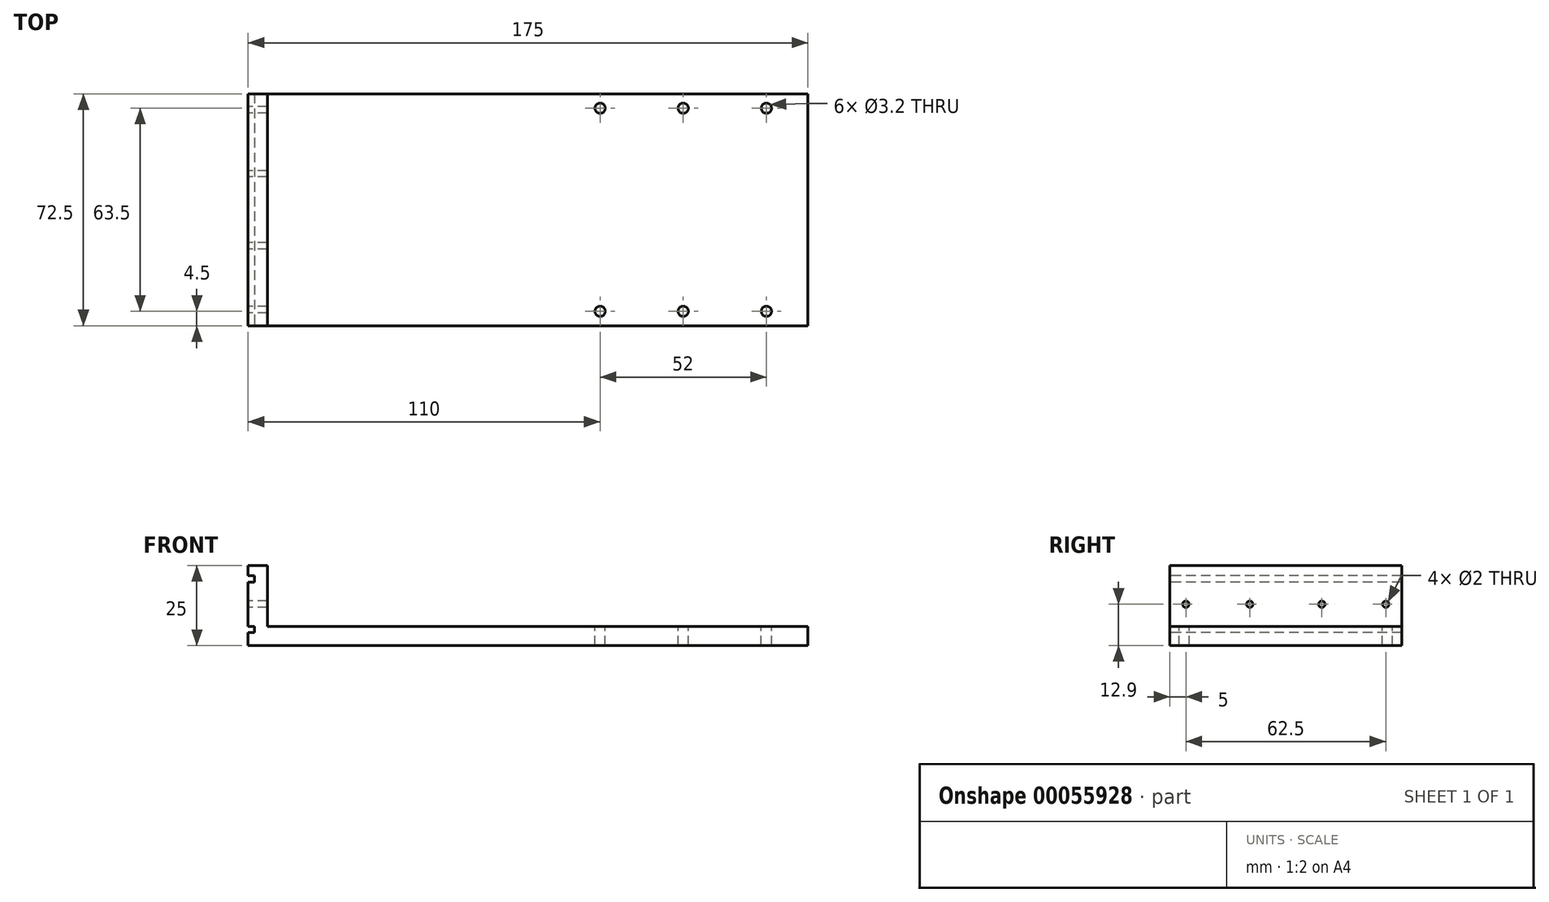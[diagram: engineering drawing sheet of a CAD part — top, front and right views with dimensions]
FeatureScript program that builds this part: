
annotation { "Feature Type Name" : "Feature", "Feature Type Description" : "" }
export const myFeature = defineFeature(function(context is Context, id is Id, definition is map)
    precondition{}
    {
        {
            var Q0;
            Q0=qCreatedBy(makeId("Top.planeOp"),FACE);
            var sketch = newSketch(context, id + "F0", { "sketchPlane" : qUnion([Q0])});
            skLineSegment(sketch, "E0.rect.bottom", {"start": v(87.5, -36.25) * mm, "end": v(-87.5, -36.25) * mm});
            skLineSegment(sketch, "E0.rect.top", {"start": v(87.5, 36.25) * mm, "end": v(-87.5, 36.25) * mm});
            skLineSegment(sketch, "E0.rect.left", {"start": v(87.5, -36.25) * mm, "end": v(87.5, 36.25) * mm});
            skLineSegment(sketch, "E0.rect.right", {"start": v(-87.5, -36.25) * mm, "end": v(-87.5, 36.25) * mm});
            skPoint(sketch, "E0.rect.middle", {"position": v(0, 0) * mm});
            skSolve(sketch);
        }
        {
            var Q0;
            Q0=makeQuery(id+"F0.imprint","IMPRINT",FACE,{"disambiguationData":[TD([[makeQuery(id+"F0.imprint","IMPRINT",EDGE,{"derivedFrom":sQuery(id+"F0.wireOp",EDGE,"E0.rect.bottom")}),-1.0]])]});
            extrude(context, id + "F1", {"entities" : qUnion([Q0]), "depth" : 25 * mm});
        }
        {
            var Q0;
            Q0=makeQuery(id+"F1.opExtrude","CAP_FACE",FACE,{"disambiguationData":[OSD([sQuery(id+"F0.wireOp",EDGE,"E0.rect.bottom"),sQuery(id+"F0.wireOp",EDGE,"E0.rect.top"),sQuery(id+"F0.wireOp",EDGE,"E0.rect.left"),sQuery(id+"F0.wireOp",EDGE,"E0.rect.right")])],"isStart":false});
            var sketch = newSketch(context, id + "F2", { "sketchPlane" : qUnion([Q0])});
            skLineSegment(sketch, "E1.bottom", {"start": v(87.5, 36.25) * mm, "end": v(-81.5, 36.25) * mm});
            skLineSegment(sketch, "E1.top", {"start": v(87.5, -36.25) * mm, "end": v(-81.5, -36.25) * mm});
            skLineSegment(sketch, "E1.left", {"start": v(87.5, 36.25) * mm, "end": v(87.5, -36.25) * mm});
            skLineSegment(sketch, "E1.right", {"start": v(-81.5, 36.25) * mm, "end": v(-81.5, -36.25) * mm});
            skSolve(sketch);
        }
        {
            var Q0;
            Q0=makeQuery(id+"F2.imprint","IMPRINT",FACE,{"disambiguationData":[TD([[makeQuery(id+"F2.imprint","IMPRINT",EDGE,{"derivedFrom":sQuery(id+"F2.wireOp",EDGE,"E1.bottom")}),1.0]])]});
            extrude(context, id + "F3", {"entities" : qUnion([Q0]), "operationType" : NewBodyOperationType.REMOVE, "oppositeDirection" : true, "depth" : 19 * mm});
        }
        {
            var Q0;
            Q0=makeQuery(id+"F3.boolean.opBoolean","COPY",FACE,{"derivedFrom":makeQuery(id+"F3.opExtrude","CAP_FACE",FACE,{"disambiguationData":[OSD([sQuery(id+"F2.wireOp",EDGE,"E1.bottom"),sQuery(id+"F2.wireOp",EDGE,"E1.top"),sQuery(id+"F2.wireOp",EDGE,"E1.left"),sQuery(id+"F2.wireOp",EDGE,"E1.right")])],"isStart":false})});
            var sketch = newSketch(context, id + "F4", { "sketchPlane" : qUnion([Q0])});
            skPoint(sketch, "E2", {"position": v(74.5, 31.75) * mm});
            skPoint(sketch, "E3", {"position": v(48.5, 31.75) * mm});
            skPoint(sketch, "E4", {"position": v(22.5, 31.75) * mm});
            skPoint(sketch, "E5.MirrorP", {"position": v(22.5, -31.75) * mm});
            skPoint(sketch, "E6.MirrorP", {"position": v(48.5, -31.75) * mm});
            skPoint(sketch, "E7.MirrorP", {"position": v(74.5, -31.75) * mm});
            skSolve(sketch);
        }
        {
            var Q0;
            Q0=sQuery(id+"F4.wireOp",VERTEX,"E4");
            var Q1;
            Q1=sQuery(id+"F4.wireOp",VERTEX,"E3");
            var Q2;
            Q2=sQuery(id+"F4.wireOp",VERTEX,"E2");
            var Q3;
            Q3=sQuery(id+"F4.wireOp",VERTEX,"E7.MirrorP");
            var Q4;
            Q4=sQuery(id+"F4.wireOp",VERTEX,"E6.MirrorP");
            var Q5;
            Q5=sQuery(id+"F4.wireOp",VERTEX,"E5.MirrorP");
            var Q6;
            Q6=makeQuery(id+"F1.opExtrude","SWEPT_BODY",BODY,{"disambiguationData":[OSD([sQuery(id+"F0.wireOp",EDGE,"E0.rect.bottom"),sQuery(id+"F0.wireOp",EDGE,"E0.rect.top"),sQuery(id+"F0.wireOp",EDGE,"E0.rect.left"),sQuery(id+"F0.wireOp",EDGE,"E0.rect.right")])]});
            hole(context, id + "F5", {"style" : HoleStyle.SIMPLE, "holeDiameter" : 3.2 * mm, "endStyle" : HoleEndStyle.THROUGH, "locations" : qUnion([Q0, Q1, Q2, Q3, Q4, Q5]), "scope" : qUnion([Q6])});
        }
        {
            var Q0;
            Q0=makeQuery(id+"F1.opExtrude","SWEPT_FACE",FACE,{"disambiguationData":[OSD([sQuery(id+"F0.wireOp",EDGE,"E0.rect.right")])]});
            var sketch = newSketch(context, id + "F6", { "sketchPlane" : qUnion([Q0])});
            skLineSegment(sketch, "E8.bottom", {"start": v(-36.25, 4) * mm, "end": v(36.25, 4) * mm});
            skLineSegment(sketch, "E8.top", {"start": v(-36.25, 6) * mm, "end": v(36.25, 6) * mm});
            skLineSegment(sketch, "E8.left", {"start": v(-36.25, 4) * mm, "end": v(-36.25, 6) * mm});
            skLineSegment(sketch, "E8.right", {"start": v(36.25, 4) * mm, "end": v(36.25, 6) * mm});
            skLineSegment(sketch, "E9.bottom", {"start": v(-36.25, 19.8) * mm, "end": v(36.25, 19.8) * mm});
            skLineSegment(sketch, "E9.top", {"start": v(-36.25, 21.8) * mm, "end": v(36.25, 21.8) * mm});
            skLineSegment(sketch, "E9.left", {"start": v(-36.25, 19.8) * mm, "end": v(-36.25, 21.8) * mm});
            skLineSegment(sketch, "E9.right", {"start": v(36.25, 19.8) * mm, "end": v(36.25, 21.8) * mm});
            skSolve(sketch);
        }
        {
            var Q0;
            Q0=makeQuery(id+"F6.imprint","IMPRINT",FACE,{"disambiguationData":[TD([[makeQuery(id+"F6.imprint","IMPRINT",EDGE,{"derivedFrom":sQuery(id+"F6.wireOp",EDGE,"E8.bottom")}),1.0]])]});
            var Q1;
            Q1=makeQuery(id+"F6.imprint","IMPRINT",FACE,{"disambiguationData":[TD([[makeQuery(id+"F6.imprint","IMPRINT",EDGE,{"derivedFrom":sQuery(id+"F6.wireOp",EDGE,"E9.bottom")}),1.0]])]});
            extrude(context, id + "F7", {"entities" : qUnion([Q0, Q1]), "operationType" : NewBodyOperationType.REMOVE, "oppositeDirection" : true, "depth" : 2 * mm});
        }
        {
            var Q0;
            Q0=makeQuery(id+"F7.boolean.opBoolean","SPLIT",FACE,{"disambiguationData":[TD([makeQuery(id+"F7.opExtrude","SWEPT_FACE",FACE,{"disambiguationData":[OSD([sQuery(id+"F6.wireOp",EDGE,"E8.top")])]})])],"derivedFrom":makeQuery(id+"F1.opExtrude","SWEPT_FACE",FACE,{"disambiguationData":[OSD([sQuery(id+"F0.wireOp",EDGE,"E0.rect.right")])]})});
            var sketch = newSketch(context, id + "F8", { "sketchPlane" : qUnion([Q0])});
            skPoint(sketch, "E10", {"position": v(-31.25, 12.9) * mm});
            skPoint(sketch, "E10.positionSnap0", {"position": v(-36.25, 12.9) * mm});
            skPoint(sketch, "E11", {"position": v(31.25, 12.9) * mm});
            skPoint(sketch, "E12", {"position": v(11.25, 12.9) * mm});
            skPoint(sketch, "E13", {"position": v(-11.25, 12.9) * mm});
            skSolve(sketch);
        }
        {
            var Q0;
            Q0=sQuery(id+"F8.wireOp",VERTEX,"E10");
            var Q1;
            Q1=sQuery(id+"F8.wireOp",VERTEX,"E13");
            var Q2;
            Q2=sQuery(id+"F8.wireOp",VERTEX,"E12");
            var Q3;
            Q3=sQuery(id+"F8.wireOp",VERTEX,"E11");
            var Q4;
            Q4=makeQuery(id+"F1.opExtrude","SWEPT_BODY",BODY,{"disambiguationData":[OSD([sQuery(id+"F0.wireOp",EDGE,"E0.rect.bottom"),sQuery(id+"F0.wireOp",EDGE,"E0.rect.top"),sQuery(id+"F0.wireOp",EDGE,"E0.rect.left"),sQuery(id+"F0.wireOp",EDGE,"E0.rect.right")])]});
            hole(context, id + "F9", {"style" : HoleStyle.SIMPLE, "holeDiameter" : 2 * mm, "endStyle" : HoleEndStyle.THROUGH, "locations" : qUnion([Q0, Q1, Q2, Q3]), "scope" : qUnion([Q4])});
        }
    });
